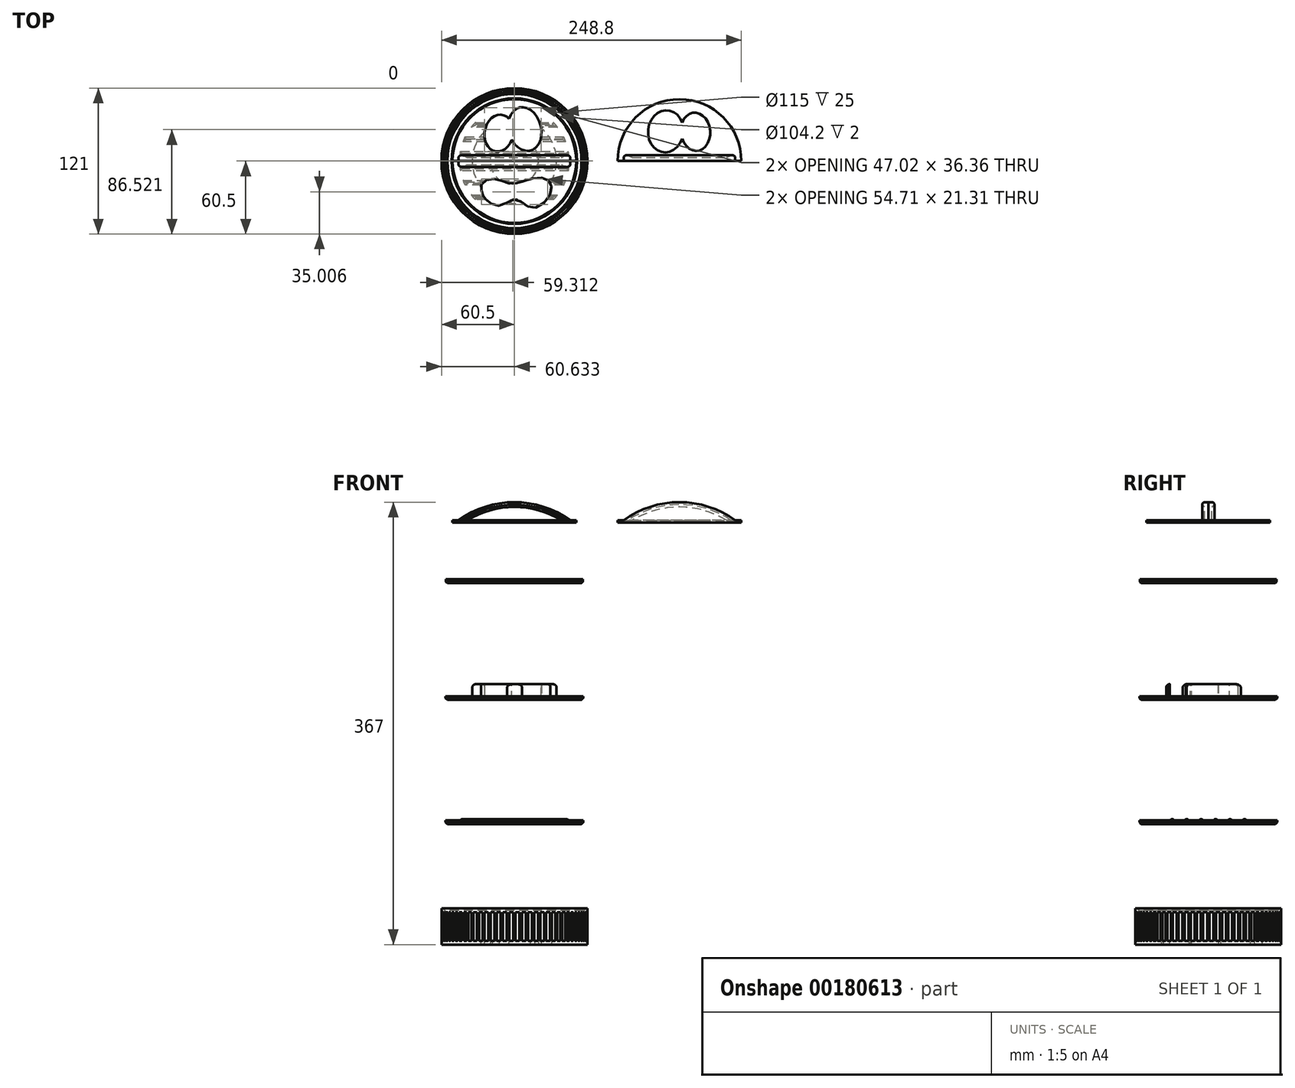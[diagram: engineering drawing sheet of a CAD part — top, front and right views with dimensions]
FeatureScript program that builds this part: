
annotation { "Feature Type Name" : "Feature", "Feature Type Description" : "" }
export const myFeature = defineFeature(function(context is Context, id is Id, definition is map)
    precondition{}
    {
        {
            var Q0;
            Q0=qCreatedBy(makeId("Top.planeOp"),FACE);
            var sketch = newSketch(context, id + "F0", { "sketchPlane" : qUnion([Q0])});
            skCircle(sketch, "E0", {"center": v(0, 0) * mm, "radius": 57.5 * mm});
            skCircle(sketch, "E1.0", {"center": v(0, 0) * mm, "radius": 60.5 * mm});
            skCircle(sketch, "E2", {"center": v(0, 0) * mm, "radius": 20 * mm});
            skSolve(sketch);
        }
        {
            var Q0;
            Q0=makeQuery(id+"F0.imprint","IMPRINT",FACE,{"disambiguationData":[TD([[makeQuery(id+"F0.imprint","IMPRINT",EDGE,{"derivedFrom":sQuery(id+"F0.wireOp",EDGE,"E0")}),1.0]])]});
            extrude(context, id + "F1", {"entities" : qUnion([Q0]), "depth" : 3 * mm});
        }
        {
            var Q0;
            Q0=makeQuery(id+"F0.imprint","IMPRINT",FACE,{"disambiguationData":[TD([[makeQuery(id+"F0.imprint","IMPRINT",EDGE,{"derivedFrom":sQuery(id+"F0.wireOp",EDGE,"E0")}),-1.0]])]});
            extrude(context, id + "F2", {"entities" : qUnion([Q0]), "operationType" : NewBodyOperationType.ADD, "depth" : 30 * mm});
        }
        {
            var Q0;
            Q0=makeQuery(id+"F2.opExtrude","CAP_EDGE",EDGE,{"disambiguationData":[OSD([sQuery(id+"F0.wireOp",EDGE,"E0")])],"isStart":false});
            chamfer(context, id + "F3", {"entities" : qUnion([Q0]), "width" : 2 * mm, "tangentPropagation" : true});
        }
        {
            var Q0;
            Q0=qCreatedBy(makeId("Top.planeOp"),FACE);
            cPlane(context, id + "F4", {"entities" : qUnion([Q0]), "cplaneType" : CPlaneType.OFFSET, "offset" : 3 * mm, "width" : 150 * mm, "height" : 150 * mm});
        }
        {
            var Q0;
            Q0=makeQuery(id+"F2.opExtrude","CAP_FACE",FACE,{"disambiguationData":[OSD([sQuery(id+"F0.wireOp",EDGE,"E0"),sQuery(id+"F0.wireOp",EDGE,"E1.0")])],"isStart":false});
            cPlane(context, id + "F5", {"entities" : qUnion([Q0]), "cplaneType" : CPlaneType.OFFSET, "offset" : 3 * mm, "oppositeDirection" : true, "width" : 150 * mm, "height" : 150 * mm});
        }
        {
            var Q0;
            Q0=qCreatedBy(id+"F4.planeOp",FACE);
            var sketch = newSketch(context, id + "F6", { "sketchPlane" : qUnion([Q0])});
            skLineSegment(sketch, "E3", {"start": v(0, 0) * mm, "end": v(0, -96.37) * mm, "construction": true});
            skLineSegment(sketch, "E4", {"start": v(0, 0) * mm, "end": v(8.18, -93.47) * mm, "construction": true});
            skLineSegment(sketch, "E5", {"start": v(0, -60.5) * mm, "end": v(1, -60.5) * mm, "construction": true});
            skLineSegment(sketch, "E6", {"start": v(5.27, -60.27) * mm, "end": v(4.28, -60.36) * mm, "construction": true});
            skCircle(sketch, "E7", {"center": v(2.7, -61.81) * mm, "radius": 2.15 * mm});
            skCircle(sketch, "E8.1.0", {"center": v(8.08, -61.34) * mm, "radius": 2.15 * mm});
            skLineSegment(sketch, "E8.1.1", {"start": v(10.5, -59.58) * mm, "end": v(9.52, -59.75) * mm, "construction": true});
            skLineSegment(sketch, "E8.1.2", {"start": v(5.27, -60.27) * mm, "end": v(6.27, -60.18) * mm, "construction": true});
            skCircle(sketch, "E8.2.0", {"center": v(13.4, -60.4) * mm, "radius": 2.15 * mm});
            skLineSegment(sketch, "E8.2.1", {"start": v(15.66, -58.44) * mm, "end": v(14.7, -58.7) * mm, "construction": true});
            skLineSegment(sketch, "E8.2.2", {"start": v(10.5, -59.58) * mm, "end": v(11.5, -59.4) * mm, "construction": true});
            skCircle(sketch, "E8.3.0", {"center": v(18.6, -59) * mm, "radius": 2.15 * mm});
            skLineSegment(sketch, "E8.3.1", {"start": v(20.7, -56.85) * mm, "end": v(19.75, -57.2) * mm, "construction": true});
            skLineSegment(sketch, "E8.3.2", {"start": v(15.66, -58.44) * mm, "end": v(16.62, -58.18) * mm, "construction": true});
            skCircle(sketch, "E8.4.0", {"center": v(23.68, -57.16) * mm, "radius": 2.15 * mm});
            skLineSegment(sketch, "E8.4.1", {"start": v(25.57, -54.83) * mm, "end": v(24.66, -55.25) * mm, "construction": true});
            skLineSegment(sketch, "E8.4.2", {"start": v(20.7, -56.85) * mm, "end": v(21.63, -56.5) * mm, "construction": true});
            skCircle(sketch, "E8.5.0", {"center": v(28.57, -54.88) * mm, "radius": 2.15 * mm});
            skLineSegment(sketch, "E8.5.1", {"start": v(30.25, -52.4) * mm, "end": v(29.38, -52.9) * mm, "construction": true});
            skLineSegment(sketch, "E8.5.2", {"start": v(25.57, -54.83) * mm, "end": v(26.47, -54.4) * mm, "construction": true});
            skCircle(sketch, "E8.6.0", {"center": v(33.24, -52.18) * mm, "radius": 2.15 * mm});
            skLineSegment(sketch, "E8.6.1", {"start": v(34.7, -49.56) * mm, "end": v(33.88, -50.13) * mm, "construction": true});
            skLineSegment(sketch, "E8.6.2", {"start": v(30.25, -52.4) * mm, "end": v(31.12, -51.9) * mm, "construction": true});
            skCircle(sketch, "E8.7.0", {"center": v(37.67, -49.09) * mm, "radius": 2.15 * mm});
            skLineSegment(sketch, "E8.7.1", {"start": v(38.89, -46.35) * mm, "end": v(38.12, -46.99) * mm, "construction": true});
            skLineSegment(sketch, "E8.7.2", {"start": v(34.7, -49.56) * mm, "end": v(35.52, -48.99) * mm, "construction": true});
            skCircle(sketch, "E8.8.0", {"center": v(41.8, -45.62) * mm, "radius": 2.15 * mm});
            skLineSegment(sketch, "E8.8.1", {"start": v(42.78, -42.78) * mm, "end": v(42.07, -43.49) * mm, "construction": true});
            skLineSegment(sketch, "E8.8.2", {"start": v(38.89, -46.35) * mm, "end": v(39.65, -45.7) * mm, "construction": true});
            skCircle(sketch, "E8.9.0", {"center": v(45.62, -41.8) * mm, "radius": 2.15 * mm});
            skLineSegment(sketch, "E8.9.1", {"start": v(46.35, -38.89) * mm, "end": v(45.7, -39.65) * mm, "construction": true});
            skLineSegment(sketch, "E8.9.2", {"start": v(42.78, -42.78) * mm, "end": v(43.49, -42.07) * mm, "construction": true});
            skCircle(sketch, "E8.10.0", {"center": v(49.09, -37.67) * mm, "radius": 2.15 * mm});
            skLineSegment(sketch, "E8.10.1", {"start": v(49.56, -34.7) * mm, "end": v(48.99, -35.52) * mm, "construction": true});
            skLineSegment(sketch, "E8.10.2", {"start": v(46.35, -38.89) * mm, "end": v(46.99, -38.12) * mm, "construction": true});
            skCircle(sketch, "E8.11.0", {"center": v(52.18, -33.24) * mm, "radius": 2.15 * mm});
            skLineSegment(sketch, "E8.11.1", {"start": v(52.4, -30.25) * mm, "end": v(51.9, -31.12) * mm, "construction": true});
            skLineSegment(sketch, "E8.11.2", {"start": v(49.56, -34.7) * mm, "end": v(50.13, -33.88) * mm, "construction": true});
            skCircle(sketch, "E8.12.0", {"center": v(54.88, -28.57) * mm, "radius": 2.15 * mm});
            skLineSegment(sketch, "E8.12.1", {"start": v(54.83, -25.57) * mm, "end": v(54.4, -26.47) * mm, "construction": true});
            skLineSegment(sketch, "E8.12.2", {"start": v(52.4, -30.25) * mm, "end": v(52.9, -29.38) * mm, "construction": true});
            skCircle(sketch, "E8.13.0", {"center": v(57.16, -23.68) * mm, "radius": 2.15 * mm});
            skLineSegment(sketch, "E8.13.1", {"start": v(56.85, -20.7) * mm, "end": v(56.5, -21.63) * mm, "construction": true});
            skLineSegment(sketch, "E8.13.2", {"start": v(54.83, -25.57) * mm, "end": v(55.25, -24.66) * mm, "construction": true});
            skCircle(sketch, "E8.14.0", {"center": v(59, -18.6) * mm, "radius": 2.15 * mm});
            skLineSegment(sketch, "E8.14.1", {"start": v(58.44, -15.66) * mm, "end": v(58.18, -16.62) * mm, "construction": true});
            skLineSegment(sketch, "E8.14.2", {"start": v(56.85, -20.7) * mm, "end": v(57.2, -19.75) * mm, "construction": true});
            skCircle(sketch, "E8.15.0", {"center": v(60.4, -13.4) * mm, "radius": 2.15 * mm});
            skLineSegment(sketch, "E8.15.1", {"start": v(59.58, -10.5) * mm, "end": v(59.4, -11.5) * mm, "construction": true});
            skLineSegment(sketch, "E8.15.2", {"start": v(58.44, -15.66) * mm, "end": v(58.7, -14.7) * mm, "construction": true});
            skCircle(sketch, "E8.16.0", {"center": v(61.34, -8.08) * mm, "radius": 2.15 * mm});
            skLineSegment(sketch, "E8.16.1", {"start": v(60.27, -5.27) * mm, "end": v(60.18, -6.27) * mm, "construction": true});
            skLineSegment(sketch, "E8.16.2", {"start": v(59.58, -10.5) * mm, "end": v(59.75, -9.52) * mm, "construction": true});
            skCircle(sketch, "E8.17.0", {"center": v(61.81, -2.7) * mm, "radius": 2.15 * mm});
            skLineSegment(sketch, "E8.17.1", {"start": v(60.5, 0) * mm, "end": v(60.5, -1) * mm, "construction": true});
            skLineSegment(sketch, "E8.17.2", {"start": v(60.27, -5.27) * mm, "end": v(60.36, -4.28) * mm, "construction": true});
            skCircle(sketch, "E8.18.0", {"center": v(61.81, 2.7) * mm, "radius": 2.15 * mm});
            skLineSegment(sketch, "E8.18.1", {"start": v(60.27, 5.27) * mm, "end": v(60.36, 4.28) * mm, "construction": true});
            skLineSegment(sketch, "E8.18.2", {"start": v(60.5, 0) * mm, "end": v(60.5, 1) * mm, "construction": true});
            skCircle(sketch, "E8.19.0", {"center": v(61.34, 8.08) * mm, "radius": 2.15 * mm});
            skLineSegment(sketch, "E8.19.1", {"start": v(59.58, 10.5) * mm, "end": v(59.75, 9.52) * mm, "construction": true});
            skLineSegment(sketch, "E8.19.2", {"start": v(60.27, 5.27) * mm, "end": v(60.18, 6.27) * mm, "construction": true});
            skCircle(sketch, "E8.20.0", {"center": v(60.4, 13.4) * mm, "radius": 2.15 * mm});
            skLineSegment(sketch, "E8.20.1", {"start": v(58.44, 15.66) * mm, "end": v(58.7, 14.7) * mm, "construction": true});
            skLineSegment(sketch, "E8.20.2", {"start": v(59.58, 10.5) * mm, "end": v(59.4, 11.5) * mm, "construction": true});
            skCircle(sketch, "E8.21.0", {"center": v(59, 18.6) * mm, "radius": 2.15 * mm});
            skLineSegment(sketch, "E8.21.1", {"start": v(56.85, 20.7) * mm, "end": v(57.2, 19.75) * mm, "construction": true});
            skLineSegment(sketch, "E8.21.2", {"start": v(58.44, 15.66) * mm, "end": v(58.18, 16.62) * mm, "construction": true});
            skCircle(sketch, "E8.22.0", {"center": v(57.16, 23.68) * mm, "radius": 2.15 * mm});
            skLineSegment(sketch, "E8.22.1", {"start": v(54.83, 25.57) * mm, "end": v(55.25, 24.66) * mm, "construction": true});
            skLineSegment(sketch, "E8.22.2", {"start": v(56.85, 20.7) * mm, "end": v(56.5, 21.63) * mm, "construction": true});
            skCircle(sketch, "E8.23.0", {"center": v(54.88, 28.57) * mm, "radius": 2.15 * mm});
            skLineSegment(sketch, "E8.23.1", {"start": v(52.4, 30.25) * mm, "end": v(52.9, 29.38) * mm, "construction": true});
            skLineSegment(sketch, "E8.23.2", {"start": v(54.83, 25.57) * mm, "end": v(54.4, 26.47) * mm, "construction": true});
            skCircle(sketch, "E8.24.0", {"center": v(52.18, 33.24) * mm, "radius": 2.15 * mm});
            skLineSegment(sketch, "E8.24.1", {"start": v(49.56, 34.7) * mm, "end": v(50.13, 33.88) * mm, "construction": true});
            skLineSegment(sketch, "E8.24.2", {"start": v(52.4, 30.25) * mm, "end": v(51.9, 31.12) * mm, "construction": true});
            skCircle(sketch, "E8.25.0", {"center": v(49.09, 37.67) * mm, "radius": 2.15 * mm});
            skLineSegment(sketch, "E8.25.1", {"start": v(46.35, 38.89) * mm, "end": v(46.99, 38.12) * mm, "construction": true});
            skLineSegment(sketch, "E8.25.2", {"start": v(49.56, 34.7) * mm, "end": v(48.99, 35.52) * mm, "construction": true});
            skCircle(sketch, "E8.26.0", {"center": v(45.62, 41.8) * mm, "radius": 2.15 * mm});
            skLineSegment(sketch, "E8.26.1", {"start": v(42.78, 42.78) * mm, "end": v(43.49, 42.07) * mm, "construction": true});
            skLineSegment(sketch, "E8.26.2", {"start": v(46.35, 38.89) * mm, "end": v(45.7, 39.65) * mm, "construction": true});
            skCircle(sketch, "E8.27.0", {"center": v(41.8, 45.62) * mm, "radius": 2.15 * mm});
            skLineSegment(sketch, "E8.27.1", {"start": v(38.89, 46.35) * mm, "end": v(39.65, 45.7) * mm, "construction": true});
            skLineSegment(sketch, "E8.27.2", {"start": v(42.78, 42.78) * mm, "end": v(42.07, 43.49) * mm, "construction": true});
            skCircle(sketch, "E8.28.0", {"center": v(37.67, 49.09) * mm, "radius": 2.15 * mm});
            skLineSegment(sketch, "E8.28.1", {"start": v(34.7, 49.56) * mm, "end": v(35.52, 48.99) * mm, "construction": true});
            skLineSegment(sketch, "E8.28.2", {"start": v(38.89, 46.35) * mm, "end": v(38.12, 46.99) * mm, "construction": true});
            skCircle(sketch, "E8.29.0", {"center": v(33.24, 52.18) * mm, "radius": 2.15 * mm});
            skLineSegment(sketch, "E8.29.1", {"start": v(30.25, 52.4) * mm, "end": v(31.12, 51.9) * mm, "construction": true});
            skLineSegment(sketch, "E8.29.2", {"start": v(34.7, 49.56) * mm, "end": v(33.88, 50.13) * mm, "construction": true});
            skCircle(sketch, "E8.30.0", {"center": v(28.57, 54.88) * mm, "radius": 2.15 * mm});
            skLineSegment(sketch, "E8.30.1", {"start": v(25.57, 54.83) * mm, "end": v(26.47, 54.4) * mm, "construction": true});
            skLineSegment(sketch, "E8.30.2", {"start": v(30.25, 52.4) * mm, "end": v(29.38, 52.9) * mm, "construction": true});
            skCircle(sketch, "E8.31.0", {"center": v(23.68, 57.16) * mm, "radius": 2.15 * mm});
            skLineSegment(sketch, "E8.31.1", {"start": v(20.7, 56.85) * mm, "end": v(21.63, 56.5) * mm, "construction": true});
            skLineSegment(sketch, "E8.31.2", {"start": v(25.57, 54.83) * mm, "end": v(24.66, 55.25) * mm, "construction": true});
            skCircle(sketch, "E8.32.0", {"center": v(18.6, 59) * mm, "radius": 2.15 * mm});
            skLineSegment(sketch, "E8.32.1", {"start": v(15.66, 58.44) * mm, "end": v(16.62, 58.18) * mm, "construction": true});
            skLineSegment(sketch, "E8.32.2", {"start": v(20.7, 56.85) * mm, "end": v(19.75, 57.2) * mm, "construction": true});
            skCircle(sketch, "E8.33.0", {"center": v(13.4, 60.4) * mm, "radius": 2.15 * mm});
            skLineSegment(sketch, "E8.33.1", {"start": v(10.5, 59.58) * mm, "end": v(11.5, 59.4) * mm, "construction": true});
            skLineSegment(sketch, "E8.33.2", {"start": v(15.66, 58.44) * mm, "end": v(14.7, 58.7) * mm, "construction": true});
            skCircle(sketch, "E8.34.0", {"center": v(8.08, 61.34) * mm, "radius": 2.15 * mm});
            skLineSegment(sketch, "E8.34.1", {"start": v(5.27, 60.27) * mm, "end": v(6.27, 60.18) * mm, "construction": true});
            skLineSegment(sketch, "E8.34.2", {"start": v(10.5, 59.58) * mm, "end": v(9.52, 59.75) * mm, "construction": true});
            skCircle(sketch, "E8.35.0", {"center": v(2.7, 61.81) * mm, "radius": 2.15 * mm});
            skLineSegment(sketch, "E8.35.1", {"start": v(0, 60.5) * mm, "end": v(1, 60.5) * mm, "construction": true});
            skLineSegment(sketch, "E8.35.2", {"start": v(5.27, 60.27) * mm, "end": v(4.28, 60.36) * mm, "construction": true});
            skCircle(sketch, "E8.36.0", {"center": v(-2.7, 61.81) * mm, "radius": 2.15 * mm});
            skLineSegment(sketch, "E8.36.1", {"start": v(-5.27, 60.27) * mm, "end": v(-4.28, 60.36) * mm, "construction": true});
            skLineSegment(sketch, "E8.36.2", {"start": v(0, 60.5) * mm, "end": v(-1, 60.5) * mm, "construction": true});
            skCircle(sketch, "E8.37.0", {"center": v(-8.08, 61.34) * mm, "radius": 2.15 * mm});
            skLineSegment(sketch, "E8.37.1", {"start": v(-10.5, 59.58) * mm, "end": v(-9.52, 59.75) * mm, "construction": true});
            skLineSegment(sketch, "E8.37.2", {"start": v(-5.27, 60.27) * mm, "end": v(-6.27, 60.18) * mm, "construction": true});
            skCircle(sketch, "E8.38.0", {"center": v(-13.4, 60.4) * mm, "radius": 2.15 * mm});
            skLineSegment(sketch, "E8.38.1", {"start": v(-15.66, 58.44) * mm, "end": v(-14.7, 58.7) * mm, "construction": true});
            skLineSegment(sketch, "E8.38.2", {"start": v(-10.5, 59.58) * mm, "end": v(-11.5, 59.4) * mm, "construction": true});
            skCircle(sketch, "E8.39.0", {"center": v(-18.6, 59) * mm, "radius": 2.15 * mm});
            skLineSegment(sketch, "E8.39.1", {"start": v(-20.7, 56.85) * mm, "end": v(-19.75, 57.2) * mm, "construction": true});
            skLineSegment(sketch, "E8.39.2", {"start": v(-15.66, 58.44) * mm, "end": v(-16.62, 58.18) * mm, "construction": true});
            skCircle(sketch, "E8.40.0", {"center": v(-23.68, 57.16) * mm, "radius": 2.15 * mm});
            skLineSegment(sketch, "E8.40.1", {"start": v(-25.57, 54.83) * mm, "end": v(-24.66, 55.25) * mm, "construction": true});
            skLineSegment(sketch, "E8.40.2", {"start": v(-20.7, 56.85) * mm, "end": v(-21.63, 56.5) * mm, "construction": true});
            skCircle(sketch, "E8.41.0", {"center": v(-28.57, 54.88) * mm, "radius": 2.15 * mm});
            skLineSegment(sketch, "E8.41.1", {"start": v(-30.25, 52.4) * mm, "end": v(-29.38, 52.9) * mm, "construction": true});
            skLineSegment(sketch, "E8.41.2", {"start": v(-25.57, 54.83) * mm, "end": v(-26.47, 54.4) * mm, "construction": true});
            skCircle(sketch, "E8.42.0", {"center": v(-33.24, 52.18) * mm, "radius": 2.15 * mm});
            skLineSegment(sketch, "E8.42.1", {"start": v(-34.7, 49.56) * mm, "end": v(-33.88, 50.13) * mm, "construction": true});
            skLineSegment(sketch, "E8.42.2", {"start": v(-30.25, 52.4) * mm, "end": v(-31.12, 51.9) * mm, "construction": true});
            skCircle(sketch, "E8.43.0", {"center": v(-37.67, 49.09) * mm, "radius": 2.15 * mm});
            skLineSegment(sketch, "E8.43.1", {"start": v(-38.89, 46.35) * mm, "end": v(-38.12, 46.99) * mm, "construction": true});
            skLineSegment(sketch, "E8.43.2", {"start": v(-34.7, 49.56) * mm, "end": v(-35.52, 48.99) * mm, "construction": true});
            skCircle(sketch, "E8.44.0", {"center": v(-41.8, 45.62) * mm, "radius": 2.15 * mm});
            skLineSegment(sketch, "E8.44.1", {"start": v(-42.78, 42.78) * mm, "end": v(-42.07, 43.49) * mm, "construction": true});
            skLineSegment(sketch, "E8.44.2", {"start": v(-38.89, 46.35) * mm, "end": v(-39.65, 45.7) * mm, "construction": true});
            skCircle(sketch, "E8.45.0", {"center": v(-45.62, 41.8) * mm, "radius": 2.15 * mm});
            skLineSegment(sketch, "E8.45.1", {"start": v(-46.35, 38.89) * mm, "end": v(-45.7, 39.65) * mm, "construction": true});
            skLineSegment(sketch, "E8.45.2", {"start": v(-42.78, 42.78) * mm, "end": v(-43.49, 42.07) * mm, "construction": true});
            skCircle(sketch, "E8.46.0", {"center": v(-49.09, 37.67) * mm, "radius": 2.15 * mm});
            skLineSegment(sketch, "E8.46.1", {"start": v(-49.56, 34.7) * mm, "end": v(-48.99, 35.52) * mm, "construction": true});
            skLineSegment(sketch, "E8.46.2", {"start": v(-46.35, 38.89) * mm, "end": v(-46.99, 38.12) * mm, "construction": true});
            skCircle(sketch, "E8.47.0", {"center": v(-52.18, 33.24) * mm, "radius": 2.15 * mm});
            skLineSegment(sketch, "E8.47.1", {"start": v(-52.4, 30.25) * mm, "end": v(-51.9, 31.12) * mm, "construction": true});
            skLineSegment(sketch, "E8.47.2", {"start": v(-49.56, 34.7) * mm, "end": v(-50.13, 33.88) * mm, "construction": true});
            skCircle(sketch, "E8.48.0", {"center": v(-54.88, 28.57) * mm, "radius": 2.15 * mm});
            skLineSegment(sketch, "E8.48.1", {"start": v(-54.83, 25.57) * mm, "end": v(-54.4, 26.47) * mm, "construction": true});
            skLineSegment(sketch, "E8.48.2", {"start": v(-52.4, 30.25) * mm, "end": v(-52.9, 29.38) * mm, "construction": true});
            skCircle(sketch, "E8.49.0", {"center": v(-57.16, 23.68) * mm, "radius": 2.15 * mm});
            skLineSegment(sketch, "E8.49.1", {"start": v(-56.85, 20.7) * mm, "end": v(-56.5, 21.63) * mm, "construction": true});
            skLineSegment(sketch, "E8.49.2", {"start": v(-54.83, 25.57) * mm, "end": v(-55.25, 24.66) * mm, "construction": true});
            skCircle(sketch, "E8.50.0", {"center": v(-59, 18.6) * mm, "radius": 2.15 * mm});
            skLineSegment(sketch, "E8.50.1", {"start": v(-58.44, 15.66) * mm, "end": v(-58.18, 16.62) * mm, "construction": true});
            skLineSegment(sketch, "E8.50.2", {"start": v(-56.85, 20.7) * mm, "end": v(-57.2, 19.75) * mm, "construction": true});
            skCircle(sketch, "E8.51.0", {"center": v(-60.4, 13.4) * mm, "radius": 2.15 * mm});
            skLineSegment(sketch, "E8.51.1", {"start": v(-59.58, 10.5) * mm, "end": v(-59.4, 11.5) * mm, "construction": true});
            skLineSegment(sketch, "E8.51.2", {"start": v(-58.44, 15.66) * mm, "end": v(-58.7, 14.7) * mm, "construction": true});
            skCircle(sketch, "E8.52.0", {"center": v(-61.34, 8.08) * mm, "radius": 2.15 * mm});
            skLineSegment(sketch, "E8.52.1", {"start": v(-60.27, 5.27) * mm, "end": v(-60.18, 6.27) * mm, "construction": true});
            skLineSegment(sketch, "E8.52.2", {"start": v(-59.58, 10.5) * mm, "end": v(-59.75, 9.52) * mm, "construction": true});
            skCircle(sketch, "E8.53.0", {"center": v(-61.81, 2.7) * mm, "radius": 2.15 * mm});
            skLineSegment(sketch, "E8.53.1", {"start": v(-60.5, 0) * mm, "end": v(-60.5, 1) * mm, "construction": true});
            skLineSegment(sketch, "E8.53.2", {"start": v(-60.27, 5.27) * mm, "end": v(-60.36, 4.28) * mm, "construction": true});
            skCircle(sketch, "E8.54.0", {"center": v(-61.81, -2.7) * mm, "radius": 2.15 * mm});
            skLineSegment(sketch, "E8.54.1", {"start": v(-60.27, -5.27) * mm, "end": v(-60.36, -4.28) * mm, "construction": true});
            skLineSegment(sketch, "E8.54.2", {"start": v(-60.5, 0) * mm, "end": v(-60.5, -1) * mm, "construction": true});
            skCircle(sketch, "E8.55.0", {"center": v(-61.34, -8.08) * mm, "radius": 2.15 * mm});
            skLineSegment(sketch, "E8.55.1", {"start": v(-59.58, -10.5) * mm, "end": v(-59.75, -9.52) * mm, "construction": true});
            skLineSegment(sketch, "E8.55.2", {"start": v(-60.27, -5.27) * mm, "end": v(-60.18, -6.27) * mm, "construction": true});
            skCircle(sketch, "E8.56.0", {"center": v(-60.4, -13.4) * mm, "radius": 2.15 * mm});
            skLineSegment(sketch, "E8.56.1", {"start": v(-58.44, -15.66) * mm, "end": v(-58.7, -14.7) * mm, "construction": true});
            skLineSegment(sketch, "E8.56.2", {"start": v(-59.58, -10.5) * mm, "end": v(-59.4, -11.5) * mm, "construction": true});
            skCircle(sketch, "E8.57.0", {"center": v(-59, -18.6) * mm, "radius": 2.15 * mm});
            skLineSegment(sketch, "E8.57.1", {"start": v(-56.85, -20.7) * mm, "end": v(-57.2, -19.75) * mm, "construction": true});
            skLineSegment(sketch, "E8.57.2", {"start": v(-58.44, -15.66) * mm, "end": v(-58.18, -16.62) * mm, "construction": true});
            skCircle(sketch, "E8.58.0", {"center": v(-57.16, -23.68) * mm, "radius": 2.15 * mm});
            skLineSegment(sketch, "E8.58.1", {"start": v(-54.83, -25.57) * mm, "end": v(-55.25, -24.66) * mm, "construction": true});
            skLineSegment(sketch, "E8.58.2", {"start": v(-56.85, -20.7) * mm, "end": v(-56.5, -21.63) * mm, "construction": true});
            skCircle(sketch, "E8.59.0", {"center": v(-54.88, -28.57) * mm, "radius": 2.15 * mm});
            skLineSegment(sketch, "E8.59.1", {"start": v(-52.4, -30.25) * mm, "end": v(-52.9, -29.38) * mm, "construction": true});
            skLineSegment(sketch, "E8.59.2", {"start": v(-54.83, -25.57) * mm, "end": v(-54.4, -26.47) * mm, "construction": true});
            skCircle(sketch, "E8.60.0", {"center": v(-52.18, -33.24) * mm, "radius": 2.15 * mm});
            skLineSegment(sketch, "E8.60.1", {"start": v(-49.56, -34.7) * mm, "end": v(-50.13, -33.88) * mm, "construction": true});
            skLineSegment(sketch, "E8.60.2", {"start": v(-52.4, -30.25) * mm, "end": v(-51.9, -31.12) * mm, "construction": true});
            skCircle(sketch, "E8.61.0", {"center": v(-49.09, -37.67) * mm, "radius": 2.15 * mm});
            skLineSegment(sketch, "E8.61.1", {"start": v(-46.35, -38.89) * mm, "end": v(-46.99, -38.12) * mm, "construction": true});
            skLineSegment(sketch, "E8.61.2", {"start": v(-49.56, -34.7) * mm, "end": v(-48.99, -35.52) * mm, "construction": true});
            skCircle(sketch, "E8.62.0", {"center": v(-45.62, -41.8) * mm, "radius": 2.15 * mm});
            skLineSegment(sketch, "E8.62.1", {"start": v(-42.78, -42.78) * mm, "end": v(-43.49, -42.07) * mm, "construction": true});
            skLineSegment(sketch, "E8.62.2", {"start": v(-46.35, -38.89) * mm, "end": v(-45.7, -39.65) * mm, "construction": true});
            skCircle(sketch, "E8.63.0", {"center": v(-41.8, -45.62) * mm, "radius": 2.15 * mm});
            skLineSegment(sketch, "E8.63.1", {"start": v(-38.89, -46.35) * mm, "end": v(-39.65, -45.7) * mm, "construction": true});
            skLineSegment(sketch, "E8.63.2", {"start": v(-42.78, -42.78) * mm, "end": v(-42.07, -43.49) * mm, "construction": true});
            skCircle(sketch, "E8.64.0", {"center": v(-37.67, -49.09) * mm, "radius": 2.15 * mm});
            skLineSegment(sketch, "E8.64.1", {"start": v(-34.7, -49.56) * mm, "end": v(-35.52, -48.99) * mm, "construction": true});
            skLineSegment(sketch, "E8.64.2", {"start": v(-38.89, -46.35) * mm, "end": v(-38.12, -46.99) * mm, "construction": true});
            skCircle(sketch, "E8.65.0", {"center": v(-33.24, -52.18) * mm, "radius": 2.15 * mm});
            skLineSegment(sketch, "E8.65.1", {"start": v(-30.25, -52.4) * mm, "end": v(-31.12, -51.9) * mm, "construction": true});
            skLineSegment(sketch, "E8.65.2", {"start": v(-34.7, -49.56) * mm, "end": v(-33.88, -50.13) * mm, "construction": true});
            skCircle(sketch, "E8.66.0", {"center": v(-28.57, -54.88) * mm, "radius": 2.15 * mm});
            skLineSegment(sketch, "E8.66.1", {"start": v(-25.57, -54.83) * mm, "end": v(-26.47, -54.4) * mm, "construction": true});
            skLineSegment(sketch, "E8.66.2", {"start": v(-30.25, -52.4) * mm, "end": v(-29.38, -52.9) * mm, "construction": true});
            skCircle(sketch, "E8.67.0", {"center": v(-23.68, -57.16) * mm, "radius": 2.15 * mm});
            skLineSegment(sketch, "E8.67.1", {"start": v(-20.7, -56.85) * mm, "end": v(-21.63, -56.5) * mm, "construction": true});
            skLineSegment(sketch, "E8.67.2", {"start": v(-25.57, -54.83) * mm, "end": v(-24.66, -55.25) * mm, "construction": true});
            skCircle(sketch, "E8.68.0", {"center": v(-18.6, -59) * mm, "radius": 2.15 * mm});
            skLineSegment(sketch, "E8.68.1", {"start": v(-15.66, -58.44) * mm, "end": v(-16.62, -58.18) * mm, "construction": true});
            skLineSegment(sketch, "E8.68.2", {"start": v(-20.7, -56.85) * mm, "end": v(-19.75, -57.2) * mm, "construction": true});
            skCircle(sketch, "E8.69.0", {"center": v(-13.4, -60.4) * mm, "radius": 2.15 * mm});
            skLineSegment(sketch, "E8.69.1", {"start": v(-10.5, -59.58) * mm, "end": v(-11.5, -59.4) * mm, "construction": true});
            skLineSegment(sketch, "E8.69.2", {"start": v(-15.66, -58.44) * mm, "end": v(-14.7, -58.7) * mm, "construction": true});
            skCircle(sketch, "E8.70.0", {"center": v(-8.08, -61.34) * mm, "radius": 2.15 * mm});
            skLineSegment(sketch, "E8.70.1", {"start": v(-5.27, -60.27) * mm, "end": v(-6.27, -60.18) * mm, "construction": true});
            skLineSegment(sketch, "E8.70.2", {"start": v(-10.5, -59.58) * mm, "end": v(-9.52, -59.75) * mm, "construction": true});
            skCircle(sketch, "E8.71.0", {"center": v(-2.7, -61.81) * mm, "radius": 2.15 * mm});
            skLineSegment(sketch, "E8.71.1", {"start": v(0, -60.5) * mm, "end": v(-1, -60.5) * mm, "construction": true});
            skLineSegment(sketch, "E8.71.2", {"start": v(-5.27, -60.27) * mm, "end": v(-4.28, -60.36) * mm, "construction": true});
            skPoint(sketch, "E8.center", {"position": v(0, 0) * mm});
            skSolve(sketch);
        }
        {
            var Q0;
            Q0 = qSketchRegion(id + "F6", true);
            var Q1;
            Q1=qCreatedBy(id+"F5.planeOp",FACE);
            extrude(context, id + "F7", {"entities" : qUnion([Q0]), "operationType" : NewBodyOperationType.REMOVE, "endBound" : BoundingType.UP_TO_SURFACE, "endBoundEntityFace" : qUnion([Q1]), "depth" : 25 * mm});
        }
        {
            var Q0;
            Q0=qCreatedBy(makeId("Top.planeOp"),FACE);
            cPlane(context, id + "F8", {"entities" : qUnion([Q0]), "cplaneType" : CPlaneType.OFFSET, "offset" : 100 * mm, "width" : 150 * mm, "height" : 150 * mm});
        }
        {
            var Q0;
            Q0=qCreatedBy(id+"F8.planeOp",FACE);
            var sketch = newSketch(context, id + "F9", { "sketchPlane" : qUnion([Q0])});
            skCircle(sketch, "E9.0", {"center": v(0, 0) * mm, "radius": 57.1 * mm});
            skSolve(sketch);
        }
        {
            var Q0;
            Q0 = qSketchRegion(id + "F9", true);
            extrude(context, id + "F10", {"entities" : qUnion([Q0]), "depth" : 3 * mm});
        }
        {
            var Q0;
            Q0=makeQuery(id+"F10.opExtrude","CAP_FACE",FACE,{"disambiguationData":[OSD([sQuery(id+"F9.wireOp",EDGE,"E9.0")])],"isStart":false});
            var sketch = newSketch(context, id + "F11", { "sketchPlane" : qUnion([Q0])});
            skLineSegment(sketch, "E10", {"start": v(0, 0) * mm, "end": v(-58.1, 0) * mm, "construction": true});
            skLineSegment(sketch, "E11", {"start": v(0, 4) * mm, "end": v(0, 8) * mm, "construction": true});
            skLineSegment(sketch, "E12", {"start": v(0, 8) * mm, "end": v(0, 16) * mm, "construction": true});
            skLineSegment(sketch, "E13", {"start": v(0, 16) * mm, "end": v(0, 20) * mm, "construction": true});
            skLineSegment(sketch, "E14", {"start": v(0, 20) * mm, "end": v(0, 28) * mm, "construction": true});
            skLineSegment(sketch, "E15", {"start": v(0, 28) * mm, "end": v(0, 32) * mm, "construction": true});
            skLineSegment(sketch, "E16", {"start": v(0, 4) * mm, "end": v(-45.32, 4) * mm});
            skLineSegment(sketch, "E17", {"start": v(0, 8) * mm, "end": v(-44.8, 8) * mm});
            skLineSegment(sketch, "E18", {"start": v(0, 16) * mm, "end": v(-42.6, 16) * mm});
            skLineSegment(sketch, "E19", {"start": v(0, 20) * mm, "end": v(-40.87, 20) * mm});
            skLineSegment(sketch, "E20", {"start": v(0, 28) * mm, "end": v(-35.86, 28) * mm});
            skLineSegment(sketch, "E21", {"start": v(0, 32) * mm, "end": v(-32.35, 32) * mm});
            skArc(sketch, "E22", {"start": v(-45.32, 4) * mm, "mid": v(-45.1, 6) * mm, "end": v(-44.8, 8) * mm});
            skArc(sketch, "E23", {"start": v(-42.6, 16) * mm, "mid": v(-41.78, 18.02) * mm, "end": v(-40.87, 20) * mm});
            skLineSegment(sketch, "E24", {"start": v(0, 4) * mm, "end": v(0, 0) * mm, "construction": true});
            skArc(sketch, "E25", {"start": v(-35.86, 28) * mm, "mid": v(-34.16, 30.05) * mm, "end": v(-32.35, 32) * mm});
            skLineSegment(sketch, "E26.MirrorCS", {"start": v(0, 32) * mm, "end": v(32.35, 32) * mm});
            skArc(sketch, "E27.MirrorCS", {"start": v(35.86, 28) * mm, "mid": v(34.16, 30.05) * mm, "end": v(32.35, 32) * mm});
            skLineSegment(sketch, "E28.MirrorCS", {"start": v(0, 28) * mm, "end": v(35.86, 28) * mm});
            skLineSegment(sketch, "E29.MirrorCS", {"start": v(0, 20) * mm, "end": v(40.87, 20) * mm});
            skArc(sketch, "E30.MirrorCS", {"start": v(42.6, 16) * mm, "mid": v(41.78, 18.02) * mm, "end": v(40.87, 20) * mm});
            skLineSegment(sketch, "E31.MirrorCS", {"start": v(0, 16) * mm, "end": v(42.6, 16) * mm});
            skLineSegment(sketch, "E32.MirrorCS", {"start": v(0, 8) * mm, "end": v(44.8, 8) * mm});
            skArc(sketch, "E33.MirrorCS", {"start": v(45.32, 4) * mm, "mid": v(45.1, 6) * mm, "end": v(44.8, 8) * mm});
            skLineSegment(sketch, "E34.MirrorCS", {"start": v(0, 4) * mm, "end": v(45.32, 4) * mm});
            skLineSegment(sketch, "E35.MirrorCS", {"start": v(0, -32) * mm, "end": v(32.35, -32) * mm});
            skArc(sketch, "E36.MirrorCS", {"start": v(45.32, -4) * mm, "mid": v(45.1, -6) * mm, "end": v(44.8, -8) * mm});
            skArc(sketch, "E37.MirrorCS", {"start": v(42.6, -16) * mm, "mid": v(41.78, -18.02) * mm, "end": v(40.87, -20) * mm});
            skLineSegment(sketch, "E38.MirrorCS", {"start": v(0, -8) * mm, "end": v(44.8, -8) * mm});
            skLineSegment(sketch, "E39.MirrorCS", {"start": v(0, -4) * mm, "end": v(45.32, -4) * mm});
            skLineSegment(sketch, "E40.MirrorCS", {"start": v(0, -32) * mm, "end": v(-32.35, -32) * mm});
            skLineSegment(sketch, "E41.MirrorCS", {"start": v(0, -16) * mm, "end": v(-42.6, -16) * mm});
            skLineSegment(sketch, "E42.MirrorCS", {"start": v(0, -8) * mm, "end": v(-44.8, -8) * mm});
            skArc(sketch, "E43.MirrorCS", {"start": v(-35.86, -28) * mm, "mid": v(-34.16, -30.05) * mm, "end": v(-32.35, -32) * mm});
            skLineSegment(sketch, "E44.MirrorCS", {"start": v(0, -20) * mm, "end": v(40.87, -20) * mm});
            skLineSegment(sketch, "E45.MirrorCS", {"start": v(0, -16) * mm, "end": v(42.6, -16) * mm});
            skArc(sketch, "E46.MirrorCS", {"start": v(-45.32, -4) * mm, "mid": v(-45.1, -6) * mm, "end": v(-44.8, -8) * mm});
            skArc(sketch, "E47.MirrorCS", {"start": v(35.86, -28) * mm, "mid": v(34.16, -30.05) * mm, "end": v(32.35, -32) * mm});
            skArc(sketch, "E48.MirrorCS", {"start": v(-42.6, -16) * mm, "mid": v(-41.78, -18.02) * mm, "end": v(-40.87, -20) * mm});
            skLineSegment(sketch, "E49.MirrorCS", {"start": v(0, -28) * mm, "end": v(-35.86, -28) * mm});
            skLineSegment(sketch, "E50.MirrorCS", {"start": v(0, -28) * mm, "end": v(35.86, -28) * mm});
            skLineSegment(sketch, "E51.MirrorCS", {"start": v(0, -20) * mm, "end": v(-40.87, -20) * mm});
            skLineSegment(sketch, "E52.MirrorCS", {"start": v(0, -4) * mm, "end": v(-45.32, -4) * mm});
            skSolve(sketch);
        }
        {
            var Q0;
            Q0 = qSketchRegion(id + "F11", true);
            extrude(context, id + "F12", {"entities" : qUnion([Q0]), "operationType" : NewBodyOperationType.ADD, "depth" : 1 * mm, "hasDraft" : true, "draftAngle" : 55 * degree, "draftPullDirection" : true});
        }
        {
            var Q0;
            Q0=makeQuery(id+"F10.opExtrude","CAP_EDGE",EDGE,{"disambiguationData":[OSD([sQuery(id+"F9.wireOp",EDGE,"E9.0")])],"isStart":true});
            chamfer(context, id + "F13", {"entities" : qUnion([Q0]), "width" : 1.4 * mm, "tangentPropagation" : true});
        }
        {
            var Q0;
            Q0=qCreatedBy(id+"F8.planeOp",FACE);
            cPlane(context, id + "F14", {"entities" : qUnion([Q0]), "cplaneType" : CPlaneType.OFFSET, "offset" : 100 * mm, "width" : 150 * mm, "height" : 150 * mm});
        }
        {
            var Q0;
            Q0=qCreatedBy(id+"F14.planeOp",FACE);
            var sketch = newSketch(context, id + "F15", { "sketchPlane" : qUnion([Q0])});
            skCircle(sketch, "E53.0", {"center": v(0, 0) * mm, "radius": 57.1 * mm});
            skSolve(sketch);
        }
        {
            var Q0;
            Q0=makeQuery(id+"F15.imprint","IMPRINT",FACE,{"disambiguationData":[TD([[makeQuery(id+"F15.imprint","IMPRINT",EDGE,{"derivedFrom":sQuery(id+"F15.wireOp",EDGE,"E53.0")}),1.0]])]});
            extrude(context, id + "F16", {"entities" : qUnion([Q0]), "depth" : 3 * mm});
        }
        {
            var Q0;
            Q0=makeQuery(id+"F16.opExtrude","CAP_FACE",FACE,{"disambiguationData":[OSD([sQuery(id+"F15.wireOp",EDGE,"E53.0")])],"isStart":true});
            var sketch = newSketch(context, id + "F17", { "sketchPlane" : qUnion([Q0])});
            skCircle(sketch, "E54", {"center": v(0, 0) * mm, "radius": 35 * mm});
            skSolve(sketch);
        }
        {
            var Q0;
            Q0=makeQuery(id+"F17.imprint","IMPRINT",FACE,{"disambiguationData":[TD([[makeQuery(id+"F17.imprint","IMPRINT",EDGE,{"derivedFrom":sQuery(id+"F17.wireOp",EDGE,"E54")}),1.0]])]});
            extrude(context, id + "F18", {"entities" : qUnion([Q0]), "operationType" : NewBodyOperationType.ADD, "depth" : 10 * mm});
        }
        {
            var Q0;
            Q0=makeQuery(id+"F18.opExtrude","CAP_EDGE",EDGE,{"disambiguationData":[OSD([sQuery(id+"F17.wireOp",EDGE,"E54")])],"isStart":true});
            var Q1;
            Q1=makeQuery(id+"F18.opExtrude","CAP_EDGE",EDGE,{"disambiguationData":[OSD([sQuery(id+"F17.wireOp",EDGE,"E54")])],"isStart":false});
            fillet(context, id + "F19", {"entities" : qUnion([Q0, Q1]), "radius" : 3 * mm, "tangentPropagation" : true, "allowEdgeOverflow" : false});
        }
        {
            var Q0;
            Q0=makeQuery(id+"F16.opExtrude","CAP_EDGE",EDGE,{"disambiguationData":[OSD([sQuery(id+"F15.wireOp",EDGE,"E53.0")])],"isStart":false});
            chamfer(context, id + "F20", {"entities" : qUnion([Q0]), "width" : 1.4 * mm, "tangentPropagation" : true});
        }
        {
            var Q0;
            Q0=makeQuery(id+"F16.opExtrude","CAP_FACE",FACE,{"disambiguationData":[OSD([sQuery(id+"F15.wireOp",EDGE,"E53.0")])],"isStart":false});
            var sketch = newSketch(context, id + "F21", { "sketchPlane" : qUnion([Q0])});
            skLineSegment(sketch, "E55", {"start": v(0, 0) * mm, "end": v(-108.36, 0) * mm, "construction": true});
            skSolve(sketch);
        }
        {
            var Q0;
            Q0=makeQuery(id+"F16.opExtrude","SWEPT_BODY",BODY,{"disambiguationData":[OSD([sQuery(id+"F15.wireOp",EDGE,"E53.0")])]});
            var Q1;
            Q1=sQuery(id+"F21.wireOp",EDGE,"E55");
            transform(context, id + "F22", {"entities" : qUnion([Q0]), "transformType" : TransformType.ROTATION, "transformAxis" : qUnion([Q1]), "angle" : 180 * degree, "makeCopy" : false});
        }
        {
            var Q0;
            Q0=qCreatedBy(id+"F14.planeOp",FACE);
            cPlane(context, id + "F23", {"entities" : qUnion([Q0]), "cplaneType" : CPlaneType.OFFSET, "offset" : 100 * mm, "width" : 150 * mm, "height" : 150 * mm});
        }
        {
            var Q0;
            Q0=qCreatedBy(id+"F23.planeOp",FACE);
            var sketch = newSketch(context, id + "F24", { "sketchPlane" : qUnion([Q0])});
            skCircle(sketch, "E56.0", {"center": v(0, 0) * mm, "radius": 56.7 * mm});
            skCircle(sketch, "E57.0", {"center": v(0, 0) * mm, "radius": 52.1 * mm});
            skSolve(sketch);
        }
        {
            var Q0;
            Q0 = qSketchRegion(id + "F24", true);
            extrude(context, id + "F25", {"entities" : qUnion([Q0]), "depth" : 2 * mm});
        }
        {
            var Q0;
            Q0=makeQuery(id+"F25.opExtrude","CAP_EDGE",EDGE,{"disambiguationData":[OSD([sQuery(id+"F24.wireOp",EDGE,"E56.0")])],"isStart":true});
            chamfer(context, id + "F26", {"entities" : qUnion([Q0]), "width" : 1 * mm, "tangentPropagation" : true});
        }
        {
            var Q0;
            Q0=makeQuery(id+"F25.opExtrude","CAP_FACE",FACE,{"disambiguationData":[OSD([sQuery(id+"F24.wireOp",EDGE,"E56.0"),sQuery(id+"F24.wireOp",EDGE,"E57.0")])],"isStart":false});
            var sketch = newSketch(context, id + "F27", { "sketchPlane" : qUnion([Q0])});
            skCircle(sketch, "E58.0", {"center": v(0, 0) * mm, "radius": 56.7 * mm});
            skCircle(sketch, "E59.0", {"center": v(0, 0) * mm, "radius": 55.7 * mm});
            skSolve(sketch);
        }
        {
            var Q0;
            Q0 = qSketchRegion(id + "F27", true);
            extrude(context, id + "F28", {"entities" : qUnion([Q0]), "operationType" : NewBodyOperationType.ADD, "depth" : 1 * mm});
        }
        {
            var Q0;
            Q0=makeQuery(id+"F28.opExtrude","CAP_EDGE",EDGE,{"disambiguationData":[OSD([sQuery(id+"F27.wireOp",EDGE,"E59.0")])],"isStart":false});
            chamfer(context, id + "F29", {"entities" : qUnion([Q0]), "width" : 1 * mm, "tangentPropagation" : true});
        }
        {
            var Q0;
            Q0=qCreatedBy(id+"F23.planeOp",FACE);
            cPlane(context, id + "F30", {"entities" : qUnion([Q0]), "cplaneType" : CPlaneType.OFFSET, "offset" : 50 * mm, "width" : 150 * mm, "height" : 150 * mm});
        }
        {
            var Q0;
            Q0=qCreatedBy(id+"F30.planeOp",FACE);
            var sketch = newSketch(context, id + "F31", { "sketchPlane" : qUnion([Q0])});
            skCircle(sketch, "E60.0", {"center": v(0, 0) * mm, "radius": 51.3 * mm, "construction": true});
            skLineSegment(sketch, "E61", {"start": v(-51.3, 0) * mm, "end": v(51.3, 0) * mm});
            skArc(sketch, "E62", {"start": v(-51.3, 0) * mm, "mid": v(0, 51.3) * mm, "end": v(51.3, 0) * mm});
            skSolve(sketch);
        }
        {
            var Q0;
            Q0 = qSketchRegion(id + "F31", true);
            extrude(context, id + "F32", {"entities" : qUnion([Q0]), "depth" : 2 * mm});
        }
        {
            var Q0;
            Q0=qCreatedBy(makeId("Front.planeOp"),FACE);
            var sketch = newSketch(context, id + "F33", { "sketchPlane" : qUnion([Q0])});
            skArc(sketch, "E63", {"start": v(46.3, 352) * mm, "mid": v(0, 367) * mm, "end": v(-46.3, 352) * mm});
            skLineSegment(sketch, "E64", {"start": v(0, 352) * mm, "end": v(0, 367) * mm, "construction": true});
            skLineSegment(sketch, "E65", {"start": v(-46.3, 352) * mm, "end": v(46.3, 352) * mm});
            skSolve(sketch);
        }
        {
            var Q0;
            Q0 = qSketchRegion(id + "F33", true);
            extrude(context, id + "F34", {"entities" : qUnion([Q0]), "operationType" : NewBodyOperationType.ADD, "oppositeDirection" : true, "depth" : 5 * mm});
        }
        {
            var Q0;
            Q0=makeQuery(id+"F34.opExtrude","CAP_FACE",FACE,{"disambiguationData":[OSD([sQuery(id+"F33.wireOp",EDGE,"E63"),sQuery(id+"F33.wireOp",EDGE,"E65")])],"isStart":false});
            var sketch = newSketch(context, id + "F35", { "sketchPlane" : qUnion([Q0])});
            skArc(sketch, "E66", {"start": v(42.8, 352) * mm, "mid": v(0, 365) * mm, "end": v(-42.8, 352) * mm});
            skSolve(sketch);
        }
        {
            var Q0;
            {var subQ0=sQuery(id+"F35.wireOp",EDGE,"E66");Q0=makeQuery(id+"F35.imprint","IMPRINT",FACE,{"disambiguationData":[TD([[makeQuery(id+"F35.imprint","IMPRINT",EDGE,{"derivedFrom":subQ0}),1.0]])]});}
            extrude(context, id + "F36", {"entities" : qUnion([Q0]), "operationType" : NewBodyOperationType.REMOVE, "oppositeDirection" : true, "depth" : 2 * mm});
        }
        {
            var Q0;
            Q0=makeQuery(id+"F36.boolean.opBoolean","COPY",EDGE,{"derivedFrom":makeQuery(id+"F36.opExtrude","CAP_EDGE",EDGE,{"disambiguationData":[OSD([sQuery(id+"F35.wireOp",EDGE,"E66")])],"isStart":false})});
            chamfer(context, id + "F37", {"entities" : qUnion([Q0]), "width" : 2 * mm, "tangentPropagation" : true});
        }
        {
            var Q0;
            Q0=makeQuery(id+"F34.opExtrude","CAP_EDGE",EDGE,{"disambiguationData":[OSD([sQuery(id+"F33.wireOp",EDGE,"E63")])],"isStart":false});
            fillet(context, id + "F38", {"entities" : qUnion([Q0]), "radius" : 2 * mm, "tangentPropagation" : true, "allowEdgeOverflow" : false});
        }
        {
            var Q0;
            Q0=makeQuery(id+"F32.opExtrude","SWEPT_BODY",BODY,{"disambiguationData":[OSD([sQuery(id+"F31.wireOp",EDGE,"E61"),sQuery(id+"F31.wireOp",EDGE,"E62")])]});
            var Q1;
            Q1=makeQuery(id+"F34.boolean.opBoolean","MERGE",FACE,{"derivedFrom":[makeQuery(id+"F32.opExtrude","SWEPT_FACE",FACE,{"disambiguationData":[OSD([sQuery(id+"F31.wireOp",EDGE,"E61")])]}),makeQuery(id+"F34.opExtrude","CAP_FACE",FACE,{"disambiguationData":[OSD([sQuery(id+"F33.wireOp",EDGE,"E63"),sQuery(id+"F33.wireOp",EDGE,"E65")])],"isStart":true})]});
            mirror(context, id + "F39", {"operationType" : NewBodyOperationType.ADD, "entities" : qUnion([Q0]), "mirrorPlane" : qUnion([Q1])});
        }
        {
            var Q0;
            Q0=makeQuery(id+"F32.opExtrude","SWEPT_BODY",BODY,{"disambiguationData":[OSD([sQuery(id+"F31.wireOp",EDGE,"E61"),sQuery(id+"F31.wireOp",EDGE,"E62")])]});
            transform(context, id + "F40", {"entities" : qUnion([Q0]), "transformType" : TransformType.TRANSLATION_3D, "dx" : 137 * mm, "dy" : 0 * mm, "dz" : 0 * mm, "makeCopy" : true});
        }
        {
            var Q0;
            {var subQ0=makeQuery(id+"F36.boolean.opBoolean","MERGE",FACE,{"derivedFrom":[makeQuery(id+"F32.opExtrude","CAP_FACE",FACE,{"disambiguationData":[OSD([sQuery(id+"F31.wireOp",EDGE,"E61"),sQuery(id+"F31.wireOp",EDGE,"E62")])],"isStart":false}),makeQuery(id+"F36.opExtrude","SWEPT_FACE",FACE,{"disambiguationData":[OSD([sQuery(id+"F33.wireOp",EDGE,"E65")])]})]});Q0=makeQuery(id+"F39.boolean.opBoolean","MERGE",FACE,{"derivedFrom":[subQ0,makeQuery(id+"F39.opPattern","COPY",FACE,{"derivedFrom":subQ0,"instanceName":"1"})]});}
            var sketch = newSketch(context, id + "F41", { "sketchPlane" : qUnion([Q0])});
            skFitSpline(sketch, "E67", {"points": [v(-27.22, -19.47) * mm, v(-17.05, -14.76) * mm, v(-2.77, -18.72) * mm, v(11.1, -15.51) * mm, v(27.4, -15.35) * mm, v(30.22, -26.44) * mm, v(15.04, -38.84) * mm, v(1.18, -31.98) * mm, v(-12.85, -37.05) * mm, v(-23.98, -31.56) * mm, v(-26.54, -27.08) * mm, v(-27.22, -19.47) * mm]});
            skEllipse(sketch, "E68", {"center": v(-12.85, 23.15) * mm, "majorRadius": 15.44 * mm, "minorRadius": 11.88 * mm, "majorAxis": v(0.18, 0.98)});
            skEllipse(sketch, "E69", {"center": v(8.7, 26.55) * mm, "majorRadius": 18.42 * mm, "minorRadius": 13.45 * mm, "majorAxis": v(0.25, -0.97)});
            skSolve(sketch);
        }
        {
            var Q0;
            Q0 = qSketchRegion(id + "F41", true);
            extrude(context, id + "F42", {"entities" : qUnion([Q0]), "operationType" : NewBodyOperationType.REMOVE, "endBound" : BoundingType.THROUGH_ALL, "oppositeDirection" : true, "depth" : 25 * mm});
        }
        {
            var Q0;
            {var subQ0=makeQuery(id+"F36.boolean.opBoolean","MERGE",FACE,{"derivedFrom":[makeQuery(id+"F32.opExtrude","CAP_FACE",FACE,{"disambiguationData":[OSD([sQuery(id+"F31.wireOp",EDGE,"E61"),sQuery(id+"F31.wireOp",EDGE,"E62")])],"isStart":false}),makeQuery(id+"F36.opExtrude","SWEPT_FACE",FACE,{"disambiguationData":[OSD([sQuery(id+"F33.wireOp",EDGE,"E65")])]})]});Q0=makeQuery(id+"F40.opPattern","COPY",FACE,{"derivedFrom":makeQuery(id+"F39.boolean.opBoolean","MERGE",FACE,{"derivedFrom":[subQ0,makeQuery(id+"F39.opPattern","COPY",FACE,{"derivedFrom":subQ0,"instanceName":"1"})]}),"instanceName":"1"});}
            var sketch = newSketch(context, id + "F43", { "sketchPlane" : qUnion([Q0])});
            skArc(sketch, "E70", {"start": v(122.12, -31) * mm, "mid": v(149.05, -31.3) * mm, "end": v(171.9, -17.04) * mm});
            skArc(sketch, "E71", {"start": v(121.35, -33.49) * mm, "mid": v(150.33, -33.74) * mm, "end": v(175.86, -20.05) * mm});
            skArc(sketch, "E72", {"start": v(154.74, -27.38) * mm, "mid": v(161.15, -24.3) * mm, "end": v(166.74, -19.9) * mm});
            skFitSpline(sketch, "E73", {"points": [v(166.74, -19.9) * mm, v(165.32, -11.6) * mm, v(157.17, -9.72) * mm, v(152.5, -20.76) * mm, v(154.74, -27.38) * mm], "startDerivative": vector(3.93, 36.72) * mm, "endDerivative": vector(12.07, -24.72) * mm});
            skFitSpline(sketch, "E74", {"points": [v(122.12, -31) * mm, v(122.12, -28.47) * mm, v(120.59, -30.4) * mm, v(119.76, -33.04) * mm, v(120.28, -34.66) * mm, v(121.35, -33.49) * mm], "startDerivative": vector(2.08, 17.16) * mm, "endDerivative": vector(6.89, 10.93) * mm});
            skFitSpline(sketch, "E75", {"points": [v(171.9, -17.04) * mm, v(171.32, -14.9) * mm, v(174.3, -15.15) * mm, v(178.05, -18.84) * mm, v(178.49, -20.95) * mm, v(175.86, -20.05) * mm], "startDerivative": vector(-7.7, 15.15) * mm, "endDerivative": vector(-17.56, 9.19) * mm});
            skEllipse(sketch, "E76", {"center": v(125.64, 24.65) * mm, "majorRadius": 17.5 * mm, "minorRadius": 14.67 * mm, "majorAxis": v(0.12, 1)});
            skEllipse(sketch, "E77", {"center": v(150.33, 24.3) * mm, "majorRadius": 15.96 * mm, "minorRadius": 12.12 * mm, "majorAxis": v(-0.11, 1)});
            skSolve(sketch);
        }
        {
            var Q0;
            Q0 = qSketchRegion(id + "F43", true);
            extrude(context, id + "F44", {"entities" : qUnion([Q0]), "operationType" : NewBodyOperationType.REMOVE, "endBound" : BoundingType.THROUGH_ALL, "oppositeDirection" : true, "depth" : 25 * mm});
        }
    });
